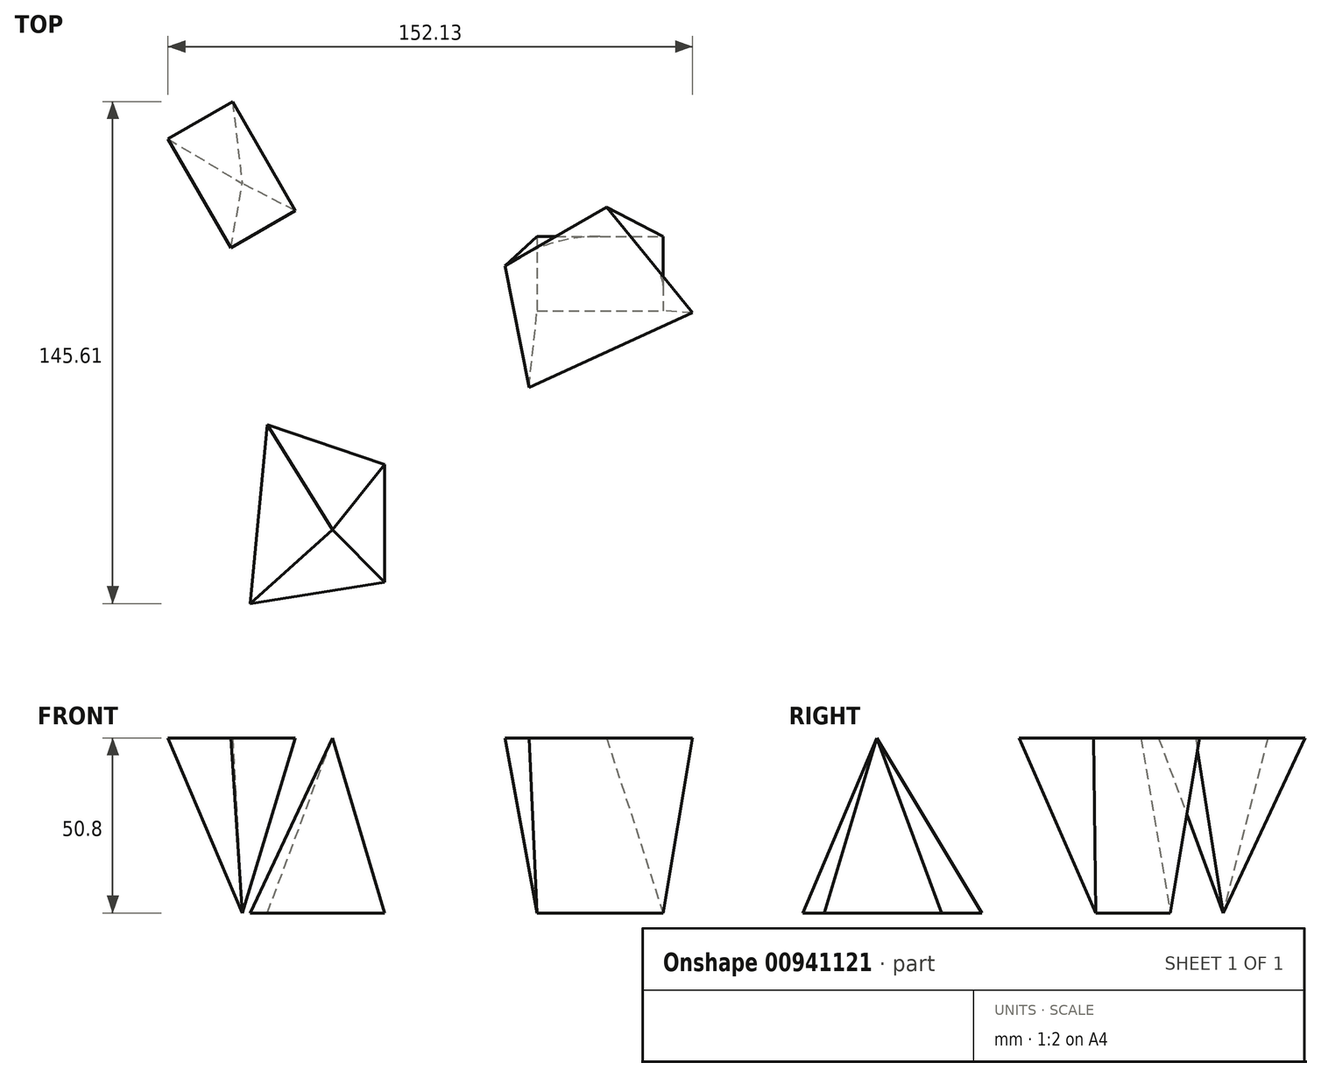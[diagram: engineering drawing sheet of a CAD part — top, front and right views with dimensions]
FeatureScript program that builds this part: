
annotation { "Feature Type Name" : "Feature", "Feature Type Description" : "" }
export const myFeature = defineFeature(function(context is Context, id is Id, definition is map)
    precondition{}
    {
        {
            var Q0;
            Q0=qCreatedBy(makeId("Top.planeOp"),FACE);
            var sketch = newSketch(context, id + "F0", { "sketchPlane" : qUnion([Q0])});
            skCircle(sketch, "E0", {"center": v(-62.28, 52.52) * mm, "radius": 11.18 * mm});
            skLineSegment(sketch, "E1.bottom", {"start": v(23.25, 37.16) * mm, "end": v(59.79, 37.16) * mm});
            skLineSegment(sketch, "E1.top", {"start": v(23.25, 15.57) * mm, "end": v(59.79, 15.57) * mm});
            skLineSegment(sketch, "E1.left", {"start": v(23.25, 37.16) * mm, "end": v(23.25, 15.57) * mm});
            skLineSegment(sketch, "E1.right", {"start": v(59.79, 37.16) * mm, "end": v(59.79, 15.57) * mm});
            skLineSegment(sketch, "E2", {"start": v(-55, -17.45) * mm, "end": v(-20.95, -29.08) * mm});
            skLineSegment(sketch, "E3", {"start": v(-20.95, -29.08) * mm, "end": v(-20.95, -63.13) * mm});
            skLineSegment(sketch, "E4", {"start": v(-20.95, -63.13) * mm, "end": v(-59.98, -69.35) * mm});
            skLineSegment(sketch, "E5", {"start": v(-59.98, -69.35) * mm, "end": v(-55, -17.45) * mm});
            skLineSegment(sketch, "E6", {"start": v(-82.91, 71.7) * mm, "end": v(-82.91, 30.26) * mm, "construction": true});
            skSolve(sketch);
        }
        {
            var Q0;
            Q0=qCreatedBy(makeId("Top.planeOp"),FACE);
            cPlane(context, id + "F1", {"entities" : qUnion([Q0]), "cplaneType" : CPlaneType.OFFSET, "offset" : 50.8 * mm, "width" : 152.4 * mm, "height" : 152.4 * mm});
        }
        {
            var Q0;
            Q0=qCreatedBy(id+"F1.planeOp",FACE);
            var sketch = newSketch(context, id + "F2", { "sketchPlane" : qUnion([Q0])});
            skCircle(sketch, "E7.0", {"center": v(-36.07, -47.94) * mm, "radius": 11.18 * mm});
            skLineSegment(sketch, "E7.1.0", {"start": v(-65.53, 33.82) * mm, "end": v(-46.83, 44.61) * mm});
            skLineSegment(sketch, "E7.1.1", {"start": v(-46.83, 44.61) * mm, "end": v(-65.1, 76.26) * mm});
            skLineSegment(sketch, "E7.1.2", {"start": v(-65.1, 76.26) * mm, "end": v(-83.8, 65.46) * mm});
            skLineSegment(sketch, "E7.1.3", {"start": v(-83.8, 65.46) * mm, "end": v(-65.53, 33.82) * mm});
            skLineSegment(sketch, "E7.2.0", {"start": v(20.9, -6.64) * mm, "end": v(68.33, 15) * mm});
            skLineSegment(sketch, "E7.2.1", {"start": v(68.33, 15) * mm, "end": v(43.42, 45.68) * mm});
            skLineSegment(sketch, "E7.2.2", {"start": v(43.42, 45.68) * mm, "end": v(13.94, 28.66) * mm});
            skLineSegment(sketch, "E7.2.3", {"start": v(13.94, 28.66) * mm, "end": v(20.9, -6.64) * mm});
            skSolve(sketch);
        }
        {
            var Q0;
            Q0=makeQuery(id+"F2.imprint","IMPRINT",FACE,{"disambiguationData":[TD([[makeQuery(id+"F2.imprint","IMPRINT",EDGE,{"derivedFrom":sQuery(id+"F2.wireOp",EDGE,"E7.2.0")}),1.0]])]});
            var Q1;
            Q1=makeQuery(id+"F0.imprint","IMPRINT",FACE,{"disambiguationData":[TD([[makeQuery(id+"F0.imprint","IMPRINT",EDGE,{"derivedFrom":sQuery(id+"F0.wireOp",EDGE,"E1.bottom")}),-1.0]])]});
            loft(context, id + "F3", {"sheetProfilesArray" : [{ "sheetProfileEntities" : qUnion([Q0]) }, { "sheetProfileEntities" : qUnion([Q1]) }]});
        }
        {
            var Q0;
            Q0=makeQuery(id+"F0.imprint","IMPRINT",FACE,{"disambiguationData":[TD([[makeQuery(id+"F0.imprint","IMPRINT",EDGE,{"derivedFrom":sQuery(id+"F0.wireOp",EDGE,"E2")}),-1.0]])]});
            var Q1;
            Q1=sQuery(id+"F2.wireOp",VERTEX,"E7.0.center");
            loft(context, id + "F4", {"sheetProfilesArray" : [{ "sheetProfileEntities" : qUnion([Q0]) }, { "sheetProfileEntities" : qUnion([Q1]) }]});
        }
        {
            var Q0;
            Q0=makeQuery(id+"F2.imprint","IMPRINT",FACE,{"disambiguationData":[TD([[makeQuery(id+"F2.imprint","IMPRINT",EDGE,{"derivedFrom":sQuery(id+"F2.wireOp",EDGE,"E7.1.0")}),1.0]])]});
            var Q1;
            Q1=sQuery(id+"F0.wireOp",VERTEX,"E0.center");
            loft(context, id + "F5", {"sheetProfilesArray" : [{ "sheetProfileEntities" : qUnion([Q0]) }, { "sheetProfileEntities" : qUnion([Q1]) }]});
        }
    });
